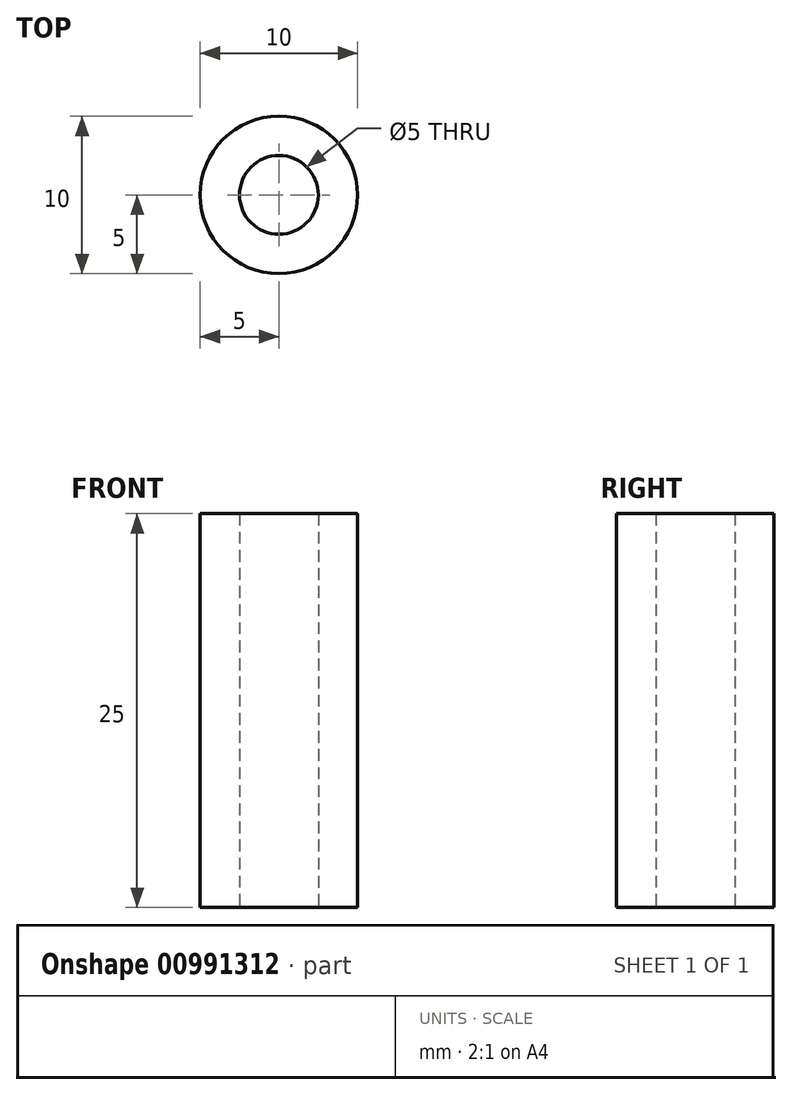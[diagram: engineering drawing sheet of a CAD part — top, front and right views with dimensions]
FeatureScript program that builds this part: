
annotation { "Feature Type Name" : "Feature", "Feature Type Description" : "" }
export const myFeature = defineFeature(function(context is Context, id is Id, definition is map)
    precondition{}
    {
        {
            var Q0;
            Q0=qCreatedBy(makeId("Top.planeOp"),FACE);
            var sketch = newSketch(context, id + "F0", { "sketchPlane" : qUnion([Q0])});
            skCircle(sketch, "E0", {"center": v(0, 0) * mm, "radius": 5 * mm});
            skCircle(sketch, "E1", {"center": v(0, 0) * mm, "radius": 2.5 * mm});
            skSolve(sketch);
        }
        {
            var Q0;
            Q0 = qSketchRegion(id + "F0", true);
            extrude(context, id + "F1", {"entities" : qUnion([Q0]), "depth" : 25 * mm, "offsetDistance" : 25 * mm});
        }
    });
